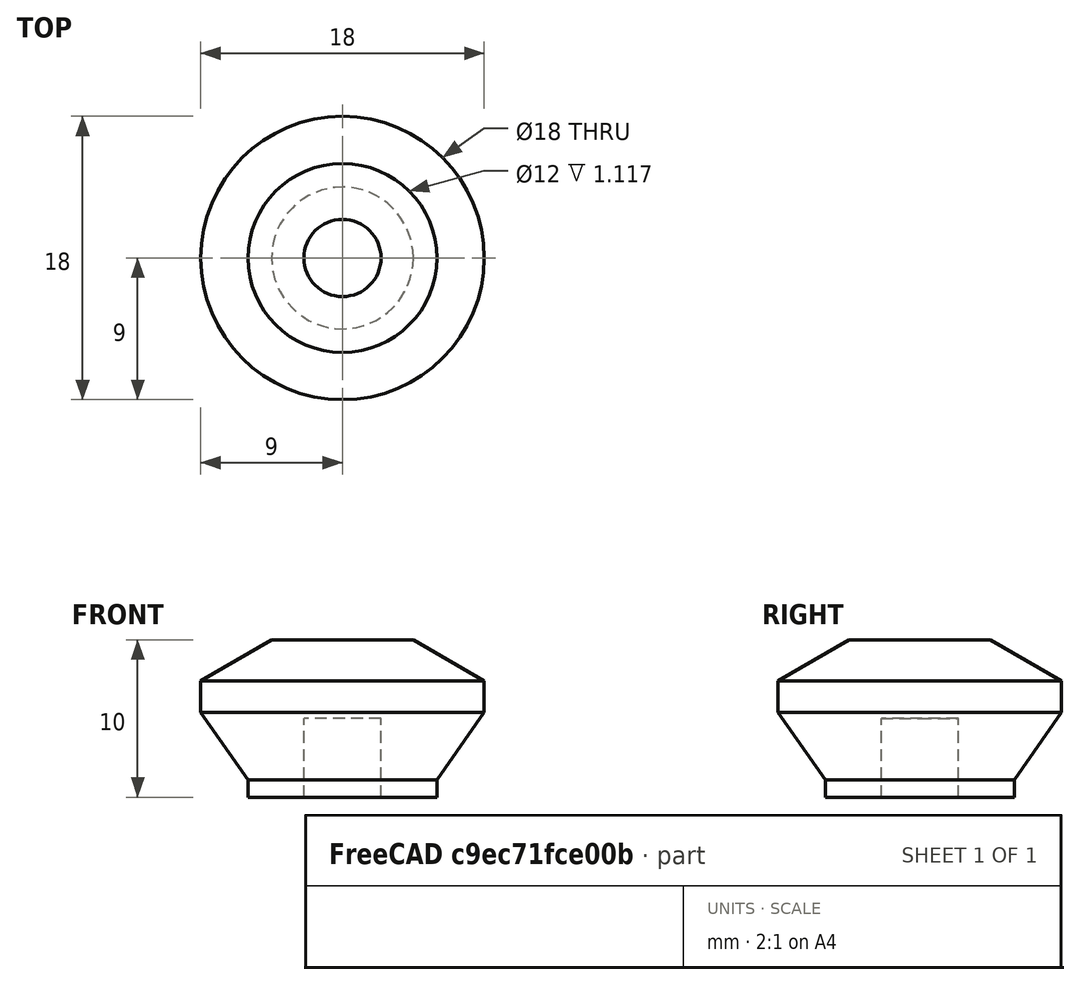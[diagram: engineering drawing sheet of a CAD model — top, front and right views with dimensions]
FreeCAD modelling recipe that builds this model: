
FCSTD DOCUMENT  (FreeCAD 0.16R6706 (Git))
Label: Static air knob
License: All rights reserved
LicenseURL: http://en.wikipedia.org/wiki/All_rights_reserved
objects: Sketcher::SketchObject×1, Part::Revolution×1
note: 2 computed .brp shape members not serialized (recipe doc carries the construction recipe); baked Part::Feature solids carry a one-line shape summary decoded from their .brp

FEATURE [Sketcher::SketchObject] Sketch
  Placement = pos=(0,0,0) rot=(1,0,0;1.5708rad)
  sketch-geometry (9):
    g0: LineSegment StartX=9 StartY=2 StartZ=0 EndX=9 EndY=0 EndZ=0
    g1: LineSegment StartX=4.5 StartY=4.59808 StartZ=0 EndX=9 EndY=2 EndZ=0
    g2: LineSegment StartX=2.45 StartY=-5.40192 StartZ=0 EndX=6 EndY=-5.40192 EndZ=0
    g3: LineSegment StartX=6 StartY=-5.40192 StartZ=0 EndX=6 EndY=-4.28444 EndZ=0
    g4: LineSegment StartX=6 StartY=-4.28444 StartZ=0 EndX=9 EndY=0 EndZ=0
    g5: LineSegment StartX=0 StartY=4.59808 StartZ=0 EndX=0 EndY=-0.401924 EndZ=0
    g6: LineSegment StartX=4.5 StartY=4.59808 StartZ=0 EndX=0 EndY=4.59808 EndZ=0
    g7: LineSegment StartX=2.45 StartY=-5.40192 StartZ=0 EndX=2.45 EndY=-0.401924 EndZ=0
    g8: LineSegment StartX=2.45 StartY=-0.401924 StartZ=0 EndX=0 EndY=-0.401924 EndZ=0
  constraints (27):
    c: PointOnObject(g0,g-1)
    c: Vertical(g0)
    c: DistanceY(g0,g0) = 2
    c: Coincident(g1,g0)
    c: Horizontal(g2)
    c: Vertical(g3)
    c: Coincident(g4,g3)
    c: Coincident(g4,g0)
    c: Coincident(g2,g3)
    c: DistanceX(g-1,g0) = 9
    c: Angle(g1,g0) = 2.0944
    c: PointOnObject(g5,g-2)
    c: Horizontal(g6)
    c: Coincident(g5,g6)
    c: Coincident(g6,g1)
    c: Angle(g0,g4) = 2.53073
    c: DistanceX(g6,g6) = 4.5
    c: Coincident(g7,g2)
    c: Vertical(g7)
    c: Coincident(g8,g7)
    c: PointOnObject(g8,g-2)
    c: Coincident(g5,g8)
    c: Horizontal(g8)
    c: DistanceY(g2,g5) = 5
    c: DistanceX(g-1,g2) = 2.45
    c: DistanceY(g5,g5) = 5
    c: DistanceX(g-1,g2) = 6
FEATURE [Part::Revolution] Revolve
  Angle = 360
  Axis = (0,0,1)
  Base = (0,0,0)
  Solid = false
  Source = -> Sketch
